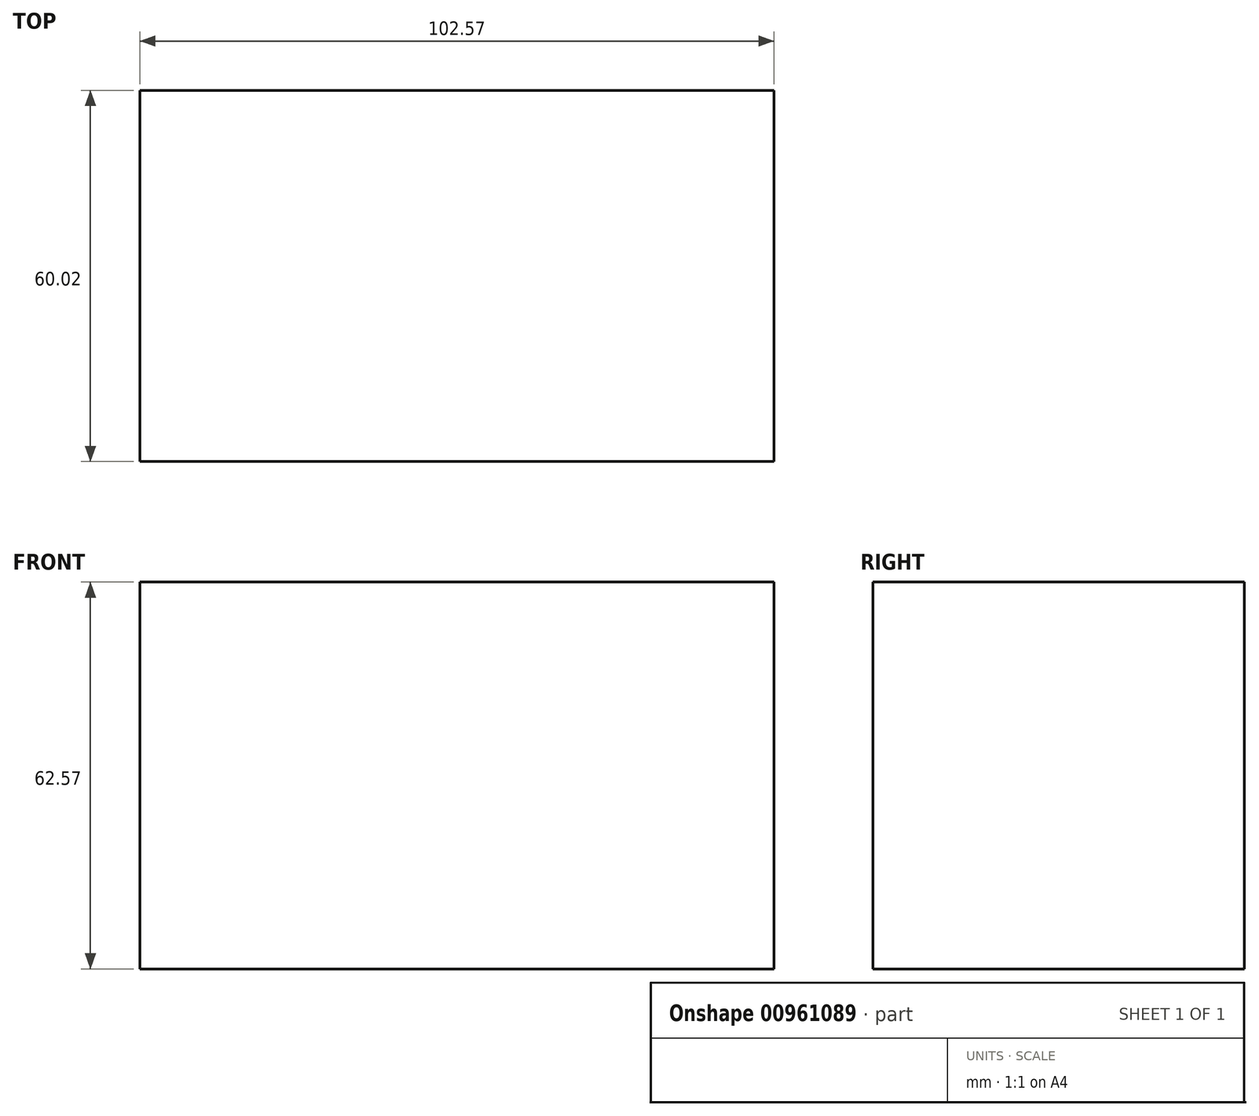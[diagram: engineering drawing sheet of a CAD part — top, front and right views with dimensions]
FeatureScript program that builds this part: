
annotation { "Feature Type Name" : "Feature", "Feature Type Description" : "" }
export const myFeature = defineFeature(function(context is Context, id is Id, definition is map)
    precondition{}
    {
        {
            var Q0;
            Q0=qCreatedBy(makeId("Front.planeOp"),FACE);
            var sketch = newSketch(context, id + "F0", { "sketchPlane" : qUnion([Q0])});
            skLineSegment(sketch, "E0.bottom", {"start": v(51.65, 32.74) * mm, "end": v(-50.92, 32.74) * mm});
            skLineSegment(sketch, "E0.top", {"start": v(51.65, -29.83) * mm, "end": v(-50.92, -29.83) * mm});
            skLineSegment(sketch, "E0.left", {"start": v(51.65, 32.74) * mm, "end": v(51.65, -29.83) * mm});
            skLineSegment(sketch, "E0.right", {"start": v(-50.92, 32.74) * mm, "end": v(-50.92, -29.83) * mm});
            skSolve(sketch);
        }
        {
            var Q0;
            Q0 = qSketchRegion(id + "F0", true);
            extrude(context, id + "F1", {"entities" : qUnion([Q0]), "depth" : 25 * mm, "offsetDistance" : 25 * mm});
        }
        {
            var Q0;
            Q0=makeQuery(id+"F1.opExtrude","CAP_FACE",FACE,{"disambiguationData":[OSD([sQuery(id+"F0.wireOp",EDGE,"E0.bottom"),sQuery(id+"F0.wireOp",EDGE,"E0.top"),sQuery(id+"F0.wireOp",EDGE,"E0.left"),sQuery(id+"F0.wireOp",EDGE,"E0.right")])],"isStart":false});
            extrude(context, id + "F2", {"entities" : qUnion([Q0]), "operationType" : NewBodyOperationType.ADD, "oppositeDirection" : true, "depth" : 60.02 * mm, "offsetDistance" : 25 * mm});
        }
    });
